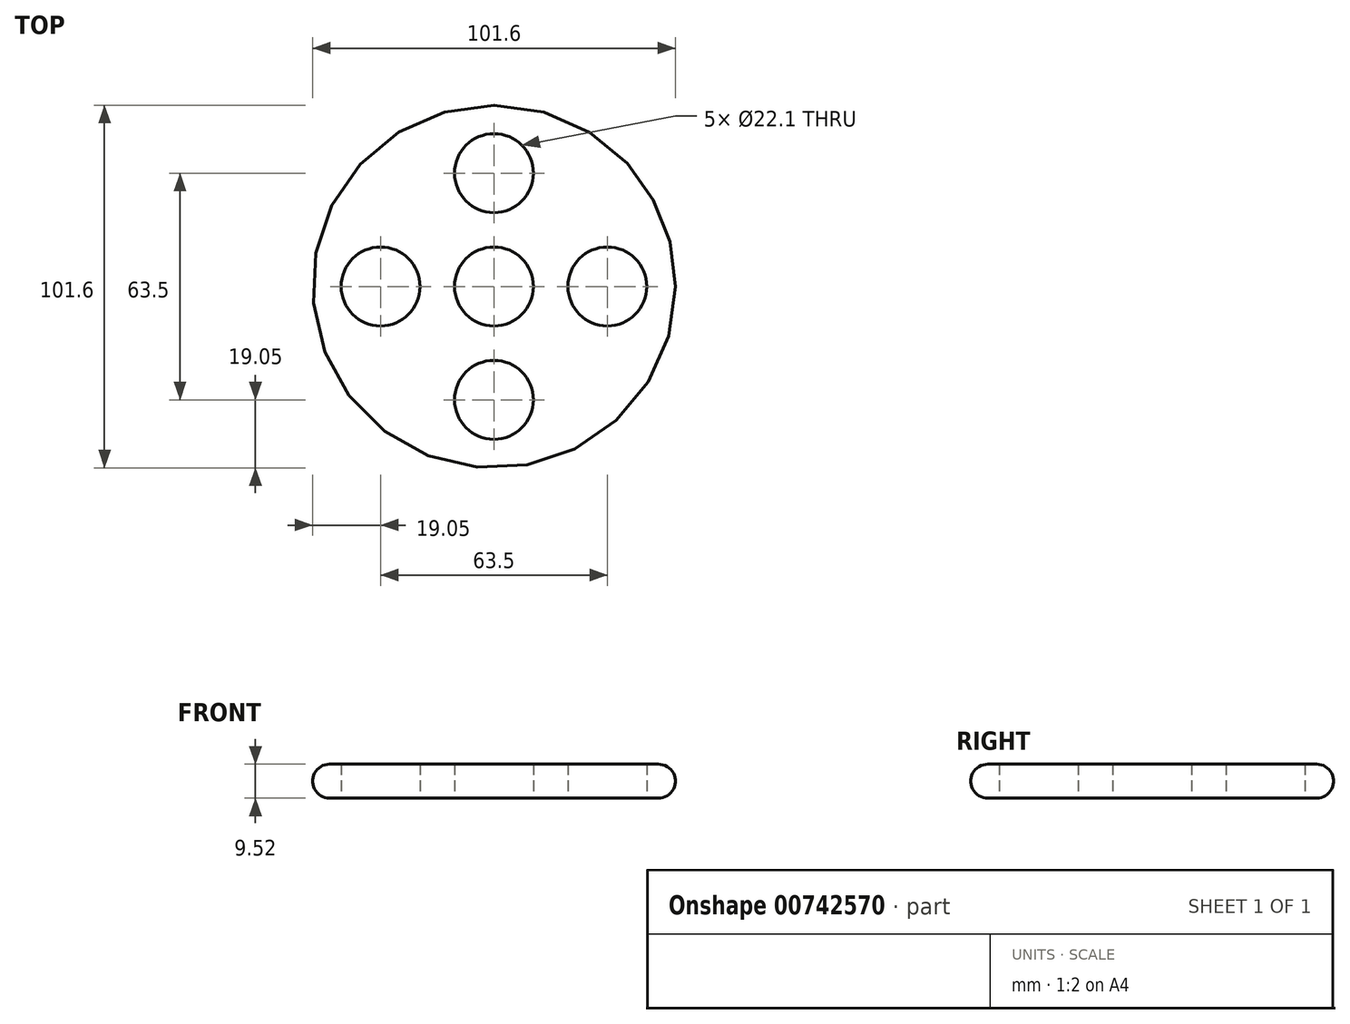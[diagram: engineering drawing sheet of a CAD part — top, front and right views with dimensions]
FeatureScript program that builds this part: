
annotation { "Feature Type Name" : "Feature", "Feature Type Description" : "" }
export const myFeature = defineFeature(function(context is Context, id is Id, definition is map)
    precondition{}
    {
        {
            var Q0;
            Q0=qCreatedBy(makeId("Top.planeOp"),FACE);
            var sketch = newSketch(context, id + "F0", { "sketchPlane" : qUnion([Q0])});
            skCircle(sketch, "E0", {"center": v(0, 0) * mm, "radius": 50.8 * mm});
            skCircle(sketch, "E1", {"center": v(0, 0) * mm, "radius": 11.05 * mm});
            skLineSegment(sketch, "E2", {"start": v(0, 0) * mm, "end": v(0, 31.75) * mm});
            skCircle(sketch, "E3", {"center": v(0, 31.75) * mm, "radius": 11.05 * mm});
            skLineSegment(sketch, "E4", {"start": v(0, 0) * mm, "end": v(31.75, 0) * mm});
            skLineSegment(sketch, "E5", {"start": v(0, 0) * mm, "end": v(0, -31.75) * mm});
            skLineSegment(sketch, "E6", {"start": v(0, 0) * mm, "end": v(-31.75, 0) * mm});
            skCircle(sketch, "E7", {"center": v(-31.75, 0) * mm, "radius": 11.05 * mm});
            skCircle(sketch, "E8", {"center": v(31.75, 0) * mm, "radius": 11.05 * mm});
            skCircle(sketch, "E9", {"center": v(0, -31.75) * mm, "radius": 11.05 * mm});
            skSolve(sketch);
        }
        {
            var Q0;
            Q0=makeQuery(id+"F0.imprint","IMPRINT",FACE,{"disambiguationData":[TD([[makeQuery(id+"F0.imprint","IMPRINT",EDGE,{"derivedFrom":sQuery(id+"F0.wireOp",EDGE,"E0")}),1.0]])]});
            extrude(context, id + "F1", {"entities" : qUnion([Q0]), "endBound" : BoundingType.SYMMETRIC, "depth" : 9.52 * mm, "offsetDistance" : 25.4 * mm});
        }
        {
            var Q0;
            Q0=makeQuery(id+"F1.opExtrude","SWEPT_FACE",FACE,{"disambiguationData":[OSD([sQuery(id+"F0.wireOp",EDGE,"E0")])]});
            fillet(context, id + "F2", {"entities" : qUnion([Q0]), "radius" : 4.76 * mm, "tangentPropagation" : true, "allowEdgeOverflow" : false});
        }
    });
